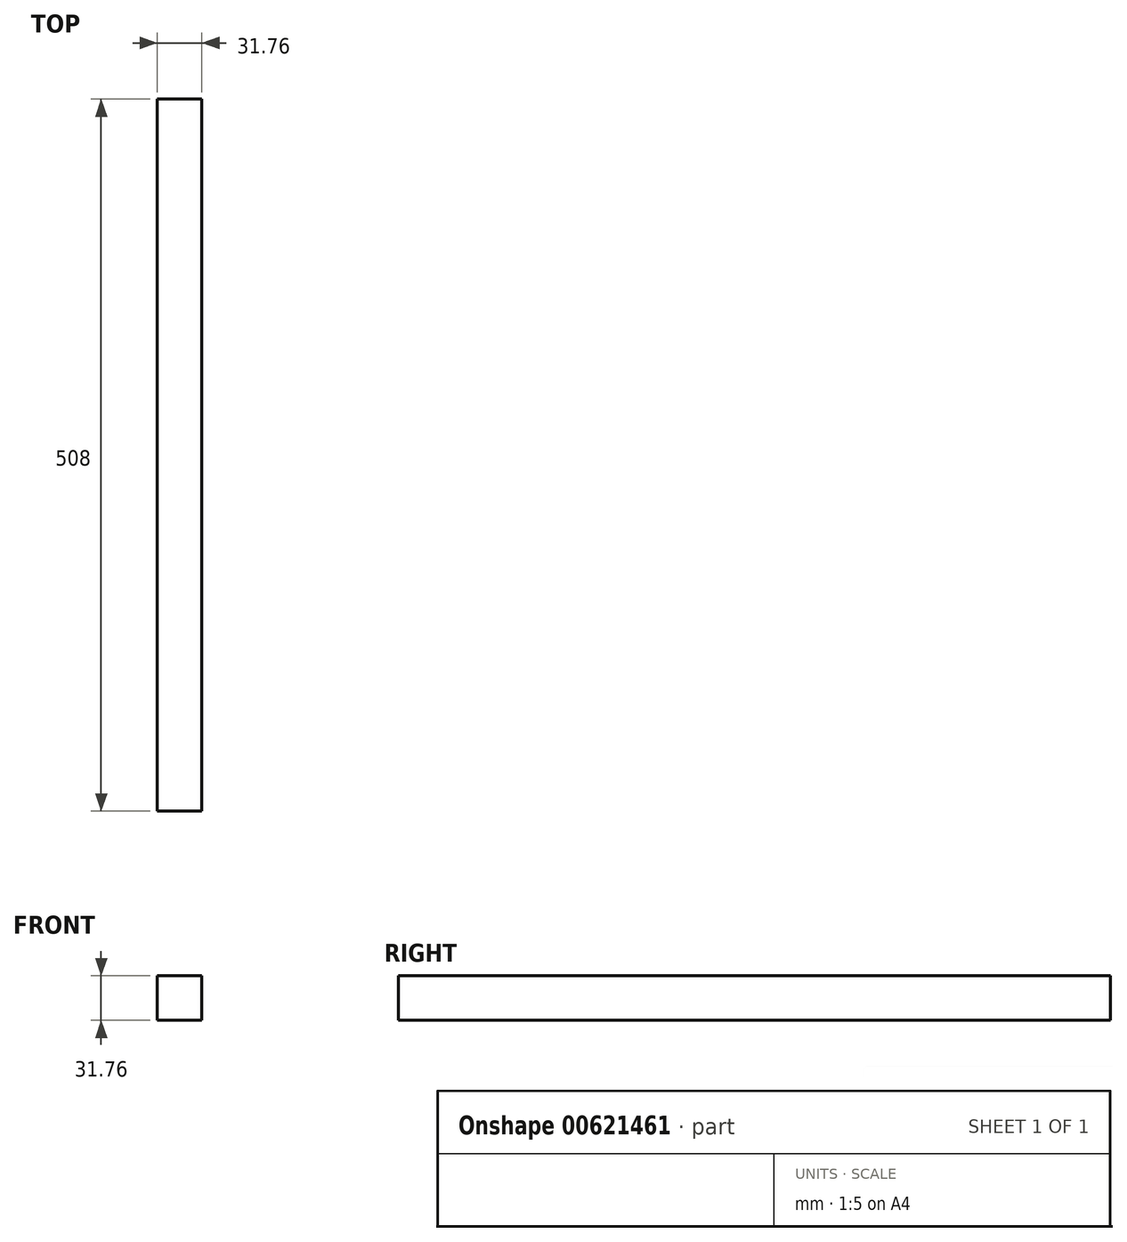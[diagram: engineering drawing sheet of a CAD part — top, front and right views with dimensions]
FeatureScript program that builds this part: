
annotation { "Feature Type Name" : "Feature", "Feature Type Description" : "" }
export const myFeature = defineFeature(function(context is Context, id is Id, definition is map)
    precondition{}
    {
        {
            var Q0;
            Q0=qCreatedBy(makeId("Front.planeOp"),FACE);
            var sketch = newSketch(context, id + "F0", { "sketchPlane" : qUnion([Q0])});
            skLineSegment(sketch, "E0.bottom", {"start": v(15.88, 15.88) * mm, "end": v(-15.88, 15.88) * mm});
            skLineSegment(sketch, "E0.top", {"start": v(15.88, -15.88) * mm, "end": v(-15.88, -15.88) * mm});
            skLineSegment(sketch, "E0.left", {"start": v(15.88, 15.88) * mm, "end": v(15.88, -15.88) * mm});
            skLineSegment(sketch, "E0.right", {"start": v(-15.88, 15.87) * mm, "end": v(-15.88, -15.88) * mm});
            skPoint(sketch, "E0.middle", {"position": v(0, 0) * mm});
            skSolve(sketch);
        }
        {
            var Q0;
            Q0 = qSketchRegion(id + "F0", true);
            extrude(context, id + "F1", {"entities" : qUnion([Q0]), "depth" : 508 * mm, "offsetDistance" : 25.4 * mm});
        }
    });
